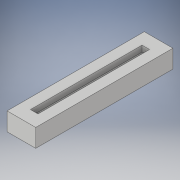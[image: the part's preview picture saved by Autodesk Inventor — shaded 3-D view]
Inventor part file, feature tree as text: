
AUTODESK INVENTOR PART (.ipt)
format: ipt  version: 2019 (Build 230136000, 136)  size: 110,592 bytes
history: native  units: mm
features: extrude x2, sketch x2, projected_geometry x1
ambient origin geometry x8: Origin, YZ Plane, XZ Plane, XY Plane, X Axis, Y Axis, Z Axis, Center Point
bodies: Solid1 (feature_tree)
feature tree (5):
  extrude  "Extrusion1"  Depth=45.5mm
  extrude  "Extrusion2"  Depth=2.5mm
  sketch  "Sketch1"  dims[d0=9.5mm d1=45.5mm]
  sketch  "Sketch2"  dims[d2=6.0mm d3=0.0mm d4=2.5mm d5=37.0mm d6=2.0mm d7=0.0mm]
  projected_geometry  "Projected Loop1"
